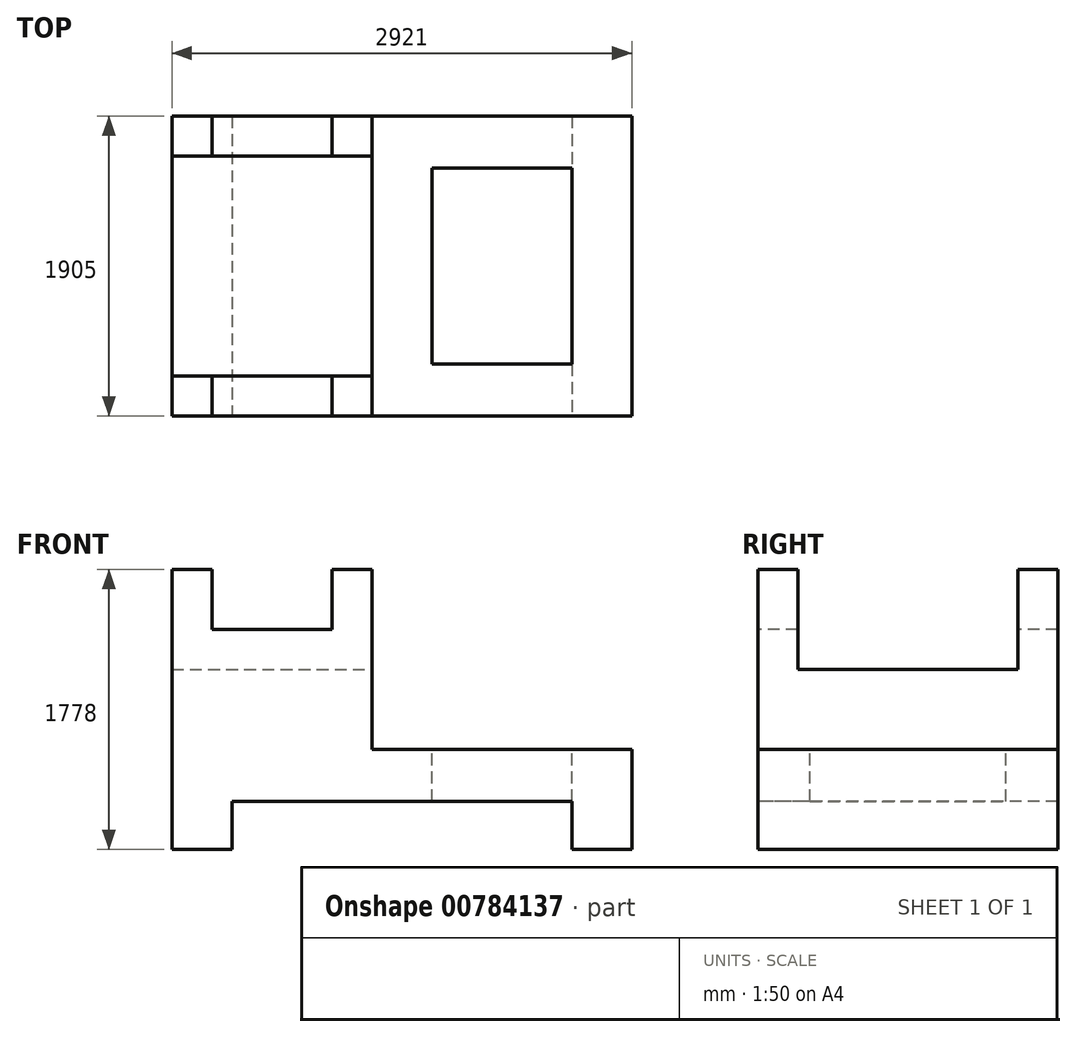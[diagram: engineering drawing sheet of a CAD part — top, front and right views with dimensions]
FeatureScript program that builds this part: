
annotation { "Feature Type Name" : "Feature", "Feature Type Description" : "" }
export const myFeature = defineFeature(function(context is Context, id is Id, definition is map)
    precondition{}
    {
        {
            var Q0;
            Q0=qCreatedBy(makeId("Front.planeOp"),FACE);
            var sketch = newSketch(context, id + "F0", { "sketchPlane" : qUnion([Q0])});
            skLineSegment(sketch, "E0.bottom", {"start": v(0, 0) * mm, "end": v(2921, 0) * mm});
            skLineSegment(sketch, "E0.top", {"start": v(0, 1778) * mm, "end": v(2921, 1778) * mm});
            skLineSegment(sketch, "E0.left", {"start": v(0, 0) * mm, "end": v(0, 1778) * mm});
            skLineSegment(sketch, "E0.right", {"start": v(2921, 0) * mm, "end": v(2921, 1778) * mm});
            skSolve(sketch);
        }
        {
            var Q0;
            Q0=qSketchRegion(id+"F0",true);
            extrude(context, id + "F1", {"entities" : qUnion([Q0]), "depth" : 1905 * mm, "offsetDistance" : 25.4 * mm});
        }
        {
            var Q0;
            Q0=makeQuery(id+"F1.opExtrude","CAP_FACE",FACE,{"disambiguationData":[OSD([sQuery(id+"F0.wireOp",EDGE,"E0.bottom"),sQuery(id+"F0.wireOp",EDGE,"E0.top"),sQuery(id+"F0.wireOp",EDGE,"E0.left"),sQuery(id+"F0.wireOp",EDGE,"E0.right")])],"isStart":false});
            var sketch = newSketch(context, id + "F2", { "sketchPlane" : qUnion([Q0])});
            skLineSegment(sketch, "E1", {"start": v(0, 0) * mm, "end": v(381, 0) * mm});
            skLineSegment(sketch, "E2", {"start": v(381, 0) * mm, "end": v(381, 304.8) * mm});
            skLineSegment(sketch, "E3", {"start": v(381, 304.8) * mm, "end": v(2540, 304.8) * mm});
            skLineSegment(sketch, "E4", {"start": v(2540, 304.8) * mm, "end": v(2540, 0) * mm});
            skLineSegment(sketch, "E5", {"start": v(2540, 0) * mm, "end": v(2921, 0) * mm});
            skSolve(sketch);
        }
        {
            var Q0;
            {var subQ0=sQuery(id+"F2.wireOp",EDGE,"E2");Q0=makeQuery(id+"F2.imprint","IMPRINT",FACE,{"disambiguationData":[TD([[makeQuery(id+"F2.imprint","IMPRINT",EDGE,{"derivedFrom":subQ0}),-1.0]])]});}
            extrude(context, id + "F3", {"entities" : qUnion([Q0]), "operationType" : NewBodyOperationType.REMOVE, "oppositeDirection" : true, "depth" : 1905 * mm, "offsetDistance" : 25.4 * mm});
        }
        {
            var Q0;
            Q0=makeQuery(id+"F1.opExtrude","CAP_FACE",FACE,{"disambiguationData":[OSD([sQuery(id+"F0.wireOp",EDGE,"E0.bottom"),sQuery(id+"F0.wireOp",EDGE,"E0.top"),sQuery(id+"F0.wireOp",EDGE,"E0.left"),sQuery(id+"F0.wireOp",EDGE,"E0.right")])],"isStart":false});
            var sketch = newSketch(context, id + "F4", { "sketchPlane" : qUnion([Q0])});
            skLineSegment(sketch, "E6", {"start": v(2921, 0) * mm, "end": v(2921, 635) * mm});
            skLineSegment(sketch, "E7", {"start": v(2921, 635) * mm, "end": v(1270, 635) * mm});
            skLineSegment(sketch, "E8", {"start": v(1270, 635) * mm, "end": v(1270, 1778) * mm});
            skSolve(sketch);
        }
        {
            var Q0;
            {var subQ0=sQuery(id+"F4.wireOp",EDGE,"E7");Q0=makeQuery(id+"F4.imprint","IMPRINT",FACE,{"disambiguationData":[TD([[makeQuery(id+"F4.imprint","IMPRINT",EDGE,{"derivedFrom":subQ0}),-1.0]])]});}
            extrude(context, id + "F5", {"entities" : qUnion([Q0]), "operationType" : NewBodyOperationType.REMOVE, "oppositeDirection" : true, "depth" : 1905 * mm, "offsetDistance" : 25.4 * mm});
        }
        {
            var Q0;
            Q0=makeQuery(id+"F1.opExtrude","CAP_FACE",FACE,{"disambiguationData":[OSD([sQuery(id+"F0.wireOp",EDGE,"E0.bottom"),sQuery(id+"F0.wireOp",EDGE,"E0.top"),sQuery(id+"F0.wireOp",EDGE,"E0.left"),sQuery(id+"F0.wireOp",EDGE,"E0.right")])],"isStart":false});
            var sketch = newSketch(context, id + "F6", { "sketchPlane" : qUnion([Q0])});
            skLineSegment(sketch, "E9", {"start": v(1270, 1778) * mm, "end": v(1016, 1778) * mm});
            skLineSegment(sketch, "E10", {"start": v(1016, 1778) * mm, "end": v(1016, 1397) * mm});
            skLineSegment(sketch, "E11", {"start": v(1016, 1397) * mm, "end": v(254, 1397) * mm});
            skLineSegment(sketch, "E12", {"start": v(254, 1397) * mm, "end": v(254, 1778) * mm});
            skLineSegment(sketch, "E13", {"start": v(254, 1778) * mm, "end": v(0, 1778) * mm});
            skLineSegment(sketch, "E14", {"start": v(0, 1778) * mm, "end": v(0, 1563.9) * mm});
            skSolve(sketch);
        }
        {
            var Q0;
            {var subQ0=sQuery(id+"F6.wireOp",EDGE,"E10");Q0=makeQuery(id+"F6.imprint","IMPRINT",FACE,{"disambiguationData":[TD([[makeQuery(id+"F6.imprint","IMPRINT",EDGE,{"derivedFrom":subQ0}),-1.0]])]});}
            extrude(context, id + "F7", {"entities" : qUnion([Q0]), "operationType" : NewBodyOperationType.REMOVE, "oppositeDirection" : true, "depth" : 1905 * mm, "offsetDistance" : 25.4 * mm});
        }
        {
            var Q0;
            Q0=makeQuery(id+"F5.boolean.opBoolean","COPY",FACE,{"derivedFrom":makeQuery(id+"F5.opExtrude","SWEPT_FACE",FACE,{"disambiguationData":[OSD([sQuery(id+"F4.wireOp",EDGE,"E8")])]})});
            var sketch = newSketch(context, id + "F8", { "sketchPlane" : qUnion([Q0])});
            skLineSegment(sketch, "E15", {"start": v(-1905, 1180.56) * mm, "end": v(-1905, 1778) * mm});
            skLineSegment(sketch, "E16", {"start": v(-1905, 1778) * mm, "end": v(-1651, 1778) * mm});
            skLineSegment(sketch, "E17", {"start": v(-1651, 1778) * mm, "end": v(-1651, 1143) * mm});
            skLineSegment(sketch, "E18", {"start": v(-1651, 1143) * mm, "end": v(-254, 1143) * mm});
            skLineSegment(sketch, "E19", {"start": v(-254, 1143) * mm, "end": v(-254, 1778) * mm});
            skLineSegment(sketch, "E20", {"start": v(-254, 1778) * mm, "end": v(0, 1778) * mm});
            skSolve(sketch);
        }
        {
            var Q0;
            {var subQ0=sQuery(id+"F8.wireOp",EDGE,"E17");Q0=makeQuery(id+"F8.imprint","IMPRINT",FACE,{"disambiguationData":[TD([[makeQuery(id+"F8.imprint","IMPRINT",EDGE,{"derivedFrom":subQ0}),1.0]])]});}
            extrude(context, id + "F9", {"entities" : qUnion([Q0]), "operationType" : NewBodyOperationType.REMOVE, "oppositeDirection" : true, "depth" : 1270 * mm, "offsetDistance" : 25.4 * mm});
        }
        {
            var Q0;
            Q0=makeQuery(id+"F5.boolean.opBoolean","COPY",FACE,{"derivedFrom":makeQuery(id+"F5.opExtrude","SWEPT_FACE",FACE,{"disambiguationData":[OSD([sQuery(id+"F4.wireOp",EDGE,"E7")])]})});
            var sketch = newSketch(context, id + "F10", { "sketchPlane" : qUnion([Q0])});
            skLineSegment(sketch, "E21", {"start": v(2019.93, 0) * mm, "end": v(2019.93, -330.2) * mm});
            skLineSegment(sketch, "E22", {"start": v(2019.93, -330.2) * mm, "end": v(2540, -330.2) * mm});
            skLineSegment(sketch, "E23", {"start": v(2540, -330.2) * mm, "end": v(2540, -1574.8) * mm});
            skLineSegment(sketch, "E24", {"start": v(2540, -1574.8) * mm, "end": v(1651, -1574.8) * mm});
            skLineSegment(sketch, "E25", {"start": v(1651, -1574.8) * mm, "end": v(1651, -330.2) * mm});
            skLineSegment(sketch, "E26", {"start": v(1651, -330.2) * mm, "end": v(2019.93, -330.2) * mm});
            skLineSegment(sketch, "E27", {"start": v(2540, -952.5) * mm, "end": v(2921, -952.5) * mm});
            skSolve(sketch);
        }
        {
            var Q0;
            {var subQ3=sQuery(id+"F10.wireOp",EDGE,"E22");Q0=makeQuery(id+"F10.imprint","IMPRINT",FACE,{"disambiguationData":[TD([[makeQuery(id+"F10.imprint","IMPRINT",EDGE,{"derivedFrom":subQ3}),-1.0]])]});}
            extrude(context, id + "F11", {"entities" : qUnion([Q0]), "operationType" : NewBodyOperationType.REMOVE, "oppositeDirection" : true, "depth" : 330.2 * mm, "offsetDistance" : 25.4 * mm});
        }
    });
